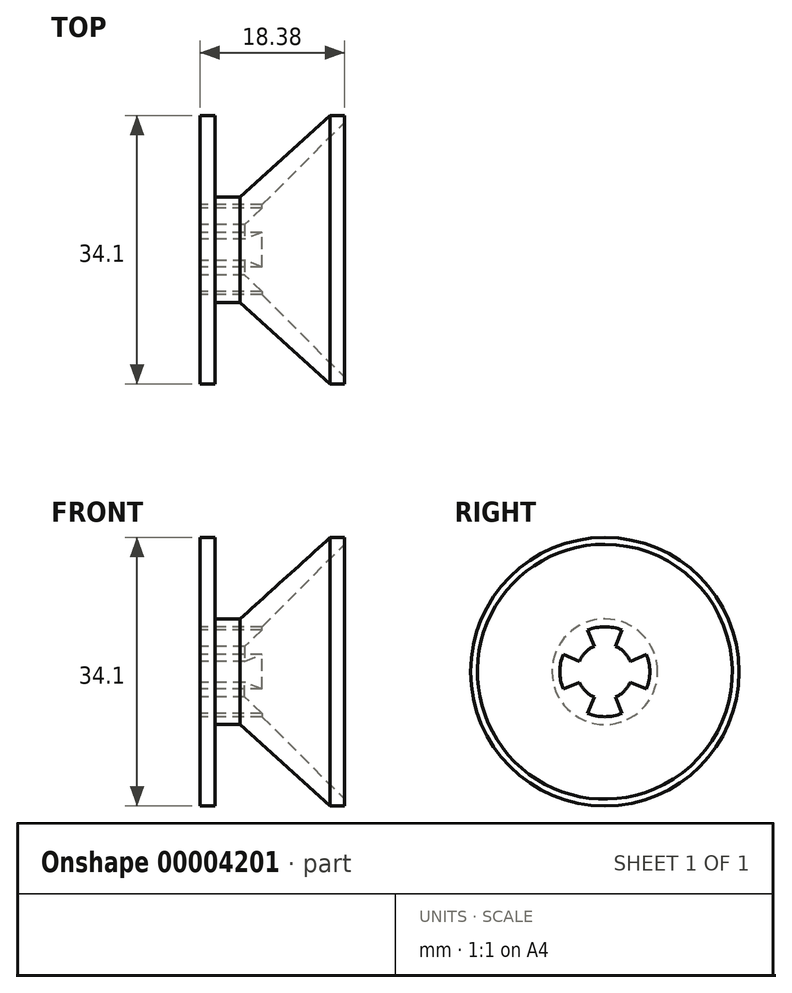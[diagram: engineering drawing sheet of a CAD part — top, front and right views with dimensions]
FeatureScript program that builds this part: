
annotation { "Feature Type Name" : "Feature", "Feature Type Description" : "" }
export const myFeature = defineFeature(function(context is Context, id is Id, definition is map)
    precondition{}
    {
        {
            var Q0;
            Q0=qCreatedBy(makeId("Front.planeOp"),FACE);
            var sketch = newSketch(context, id + "F0", { "sketchPlane" : qUnion([Q0])});
            skPoint(sketch, "E0", {"position": v(16.68, 17.05) * mm});
            skLineSegment(sketch, "E1", {"start": v(0, 0) * mm, "end": v(7.84, 0) * mm});
            skLineSegment(sketch, "E2", {"start": v(2.04, 6.7) * mm, "end": v(5.21, 6.7) * mm});
            skLineSegment(sketch, "E3", {"start": v(16.68, 17.05) * mm, "end": v(5.21, 6.7) * mm});
            skPoint(sketch, "E4.visualSharp", {"position": v(2.04, 17.05) * mm});
            skLineSegment(sketch, "E5", {"start": v(2.04, 6.7) * mm, "end": v(2.04, 17.05) * mm});
            skLineSegment(sketch, "E6", {"start": v(0.13, 17.05) * mm, "end": v(2.04, 17.05) * mm});
            skLineSegment(sketch, "E7", {"start": v(18.51, 16.19) * mm, "end": v(18.51, 17.05) * mm});
            skLineSegment(sketch, "E8", {"start": v(18.51, 17.05) * mm, "end": v(16.68, 17.05) * mm});
            skLineSegment(sketch, "E9", {"start": v(0.13, 3.5) * mm, "end": v(5.82, 3.5) * mm});
            skLineSegment(sketch, "E10", {"start": v(5.82, 3.5) * mm, "end": v(18.51, 16.19) * mm});
            skLineSegment(sketch, "E11", {"start": v(0.13, 17.05) * mm, "end": v(0.13, 3.5) * mm});
            skSolve(sketch);
        }
        {
            var Q0;
            Q0=makeQuery(id+"F0.imprint","IMPRINT",FACE,{"disambiguationData":[TD([[makeQuery(id+"F0.imprint","IMPRINT",EDGE,{"derivedFrom":sQuery(id+"F0.wireOp",EDGE,"E2")}),-1.0]])]});
            var Q1;
            Q1=sQuery(id+"F0.wireOp",EDGE,"E1");
            revolve(context, id + "F1", {"entities" : qUnion([Q0]), "axis" : qUnion([Q1]), "revolveType" : RevolveType.FULL});
        }
        {
            var Q0;
            Q0=makeQuery(id+"F1.opRevolve","SWEPT_FACE",FACE,{"disambiguationData":[OSD([sQuery(id+"F0.wireOp",EDGE,"E11")])]});
            var sketch = newSketch(context, id + "F2", { "sketchPlane" : qUnion([Q0])});
            skArc(sketch, "E12", {"start": v(3.23, -1.34) * mm, "mid": v(3.5, 0) * mm, "end": v(3.23, 1.34) * mm});
            skArc(sketch, "E13", {"start": v(-1.34, -3.23) * mm, "mid": v(0, -3.5) * mm, "end": v(1.34, -3.23) * mm});
            skArc(sketch, "E14", {"start": v(-3.23, 1.34) * mm, "mid": v(-3.5, 0) * mm, "end": v(-3.23, -1.34) * mm});
            skArc(sketch, "E15", {"start": v(1.34, 3.23) * mm, "mid": v(0, 3.5) * mm, "end": v(-1.34, 3.23) * mm});
            skLineSegment(sketch, "E16", {"start": v(-5.28, 2.19) * mm, "end": v(-3.23, 1.34) * mm});
            skLineSegment(sketch, "E17", {"start": v(-1.34, 3.23) * mm, "end": v(-2.19, 5.28) * mm});
            skLineSegment(sketch, "E18", {"start": v(2.19, 5.28) * mm, "end": v(1.34, 3.23) * mm});
            skLineSegment(sketch, "E19", {"start": v(3.23, 1.34) * mm, "end": v(5.28, 2.19) * mm});
            skLineSegment(sketch, "E20", {"start": v(3.23, -1.34) * mm, "end": v(5.28, -2.19) * mm});
            skLineSegment(sketch, "E21", {"start": v(1.34, -3.23) * mm, "end": v(2.19, -5.28) * mm});
            skLineSegment(sketch, "E22", {"start": v(-1.34, -3.23) * mm, "end": v(-2.19, -5.28) * mm});
            skLineSegment(sketch, "E23", {"start": v(-3.23, -1.34) * mm, "end": v(-5.28, -2.19) * mm});
            skArc(sketch, "E24", {"start": v(-5.28, 2.19) * mm, "mid": v(-5.72, 0) * mm, "end": v(-5.28, -2.19) * mm});
            skArc(sketch, "E25", {"start": v(-2.19, -5.28) * mm, "mid": v(0, -5.72) * mm, "end": v(2.19, -5.28) * mm});
            skArc(sketch, "E26", {"start": v(5.28, -2.19) * mm, "mid": v(5.72, 0) * mm, "end": v(5.28, 2.19) * mm});
            skArc(sketch, "E27", {"start": v(2.19, 5.28) * mm, "mid": v(0, 5.72) * mm, "end": v(-2.19, 5.28) * mm});
            skSolve(sketch);
        }
        {
            var Q0;
            Q0 = qSketchRegion(id + "F2", true);
            extrude(context, id + "F3", {"entities" : qUnion([Q0]), "operationType" : NewBodyOperationType.REMOVE, "endBound" : BoundingType.UP_TO_NEXT, "oppositeDirection" : true, "depth" : 25.4 * mm});
        }
    });
